# Revit family: ARKOSLIGHT_Black Foster GAP
name_source: partatom
category: Lighting Fixtures
units: mm (PartAtom-declared; Revit-internal decimal feet)

## family parameters
Cut with Voids When Loaded = No
Host = Face
Light Source = No
Part Type = Normal
Room Calculation Point = No
Round Connector Dimension = Use Diameter
Shared = No

## types (4) — shared parameters
ARKOSLIGHT_Color = Black
ARKOSLIGHT_Fixture Type = ACCESSORIES
ARKOSLIGHT_Model = ACCESSORIES
ARKOSLIGHT_Series = BLACK FOSTER ACCESSORIES
Apparent Load = 4 VA
Manufacturer = ARKOSLIGHT
Model = ACCESSORIES
URL = https://www.arkoslight.com
zero-valued in all types: Default Elevation

## per-type parameters (varying)
| type | ARKOSLIGHT_Reference | Length |
| A3170001N - BLACK FOSTER GAP 250 N | A3170001N | 250 mm  [stored 0.82021 ft] |
| A3170002N - BLACK FOSTER GAP 500 N | A3170002N | 500 mm  [stored 1.64042 ft] |
| A3170003N - BLACK FOSTER GAP 1000 N | A3170003N | 1000 mm  [stored 3.28084 ft] |
| A3170004N - BLACK FOSTER GAP 2000 N | A3170004N | 2000 mm  [stored 6.56168 ft] |

note: [stored X ft] marks values corroborated as IEEE doubles in the binary element streams (Revit-internal decimal feet)

## geometry (parser evidence)
native form markers: Sweep x2
no freeform markers — native parametric forms only
